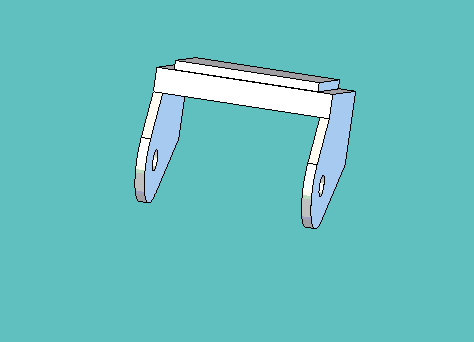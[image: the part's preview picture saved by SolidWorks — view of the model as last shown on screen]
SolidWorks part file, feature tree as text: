
SOLIDWORKS PART (.sldprt)
format: sldprt  version: not decoded by parser v0  size: 294,912 bytes
history: native  units: mm
features: sketch x4, extrude x4, material x1 (+11 scaffold rows collapsed)
feature tree (20):
  scaffold x11  (default folders/planes/origin — collapsed)
  material  "Material <not specified>"
  sketch  "Sketch1"  dims[D1=38.1mm D2=25.4mm]
  extrude  "Extrude1"  Depth=2.38125mm
  sketch  "Sketch2"  dims[D1=1.5875mm D2=1.5875mm D3=4.2672mm D4=4.2672mm]
  extrude  "Extrude2"  Depth=6.35mm
  sketch  "Sketch3"  dims[c1.D2=3.175mm c1.D7=22.225mm c1.D4=~5.55625mm c1.D6=22.225mm c1.D1=47.625mm c1.D3=9.525mm c2.D4=6.35mm c2.D5=12.7mm c2.D6=23.8125mm c2.D1=~76.493677mm c3.D1=45.0deg c3.D2=~33.742581mm c4.D2=~55.024647deg c4.D3=66.9114mm c4.D1=~26.19375mm c5.D3=17.4625mm]
  extrude  "Extrude3"  Depth=2.4892mm
  sketch  "Sketch4"  dims[D1=0.0mm]
  extrude  "Extrude4"  Depth=2.4892mm
decode coverage: 8 of 8 modeling features carry decoded parameters
note: ~ marks probable driven/reference dimensions
note: suppression state not decoded; provenance and decode notes live in map.json
